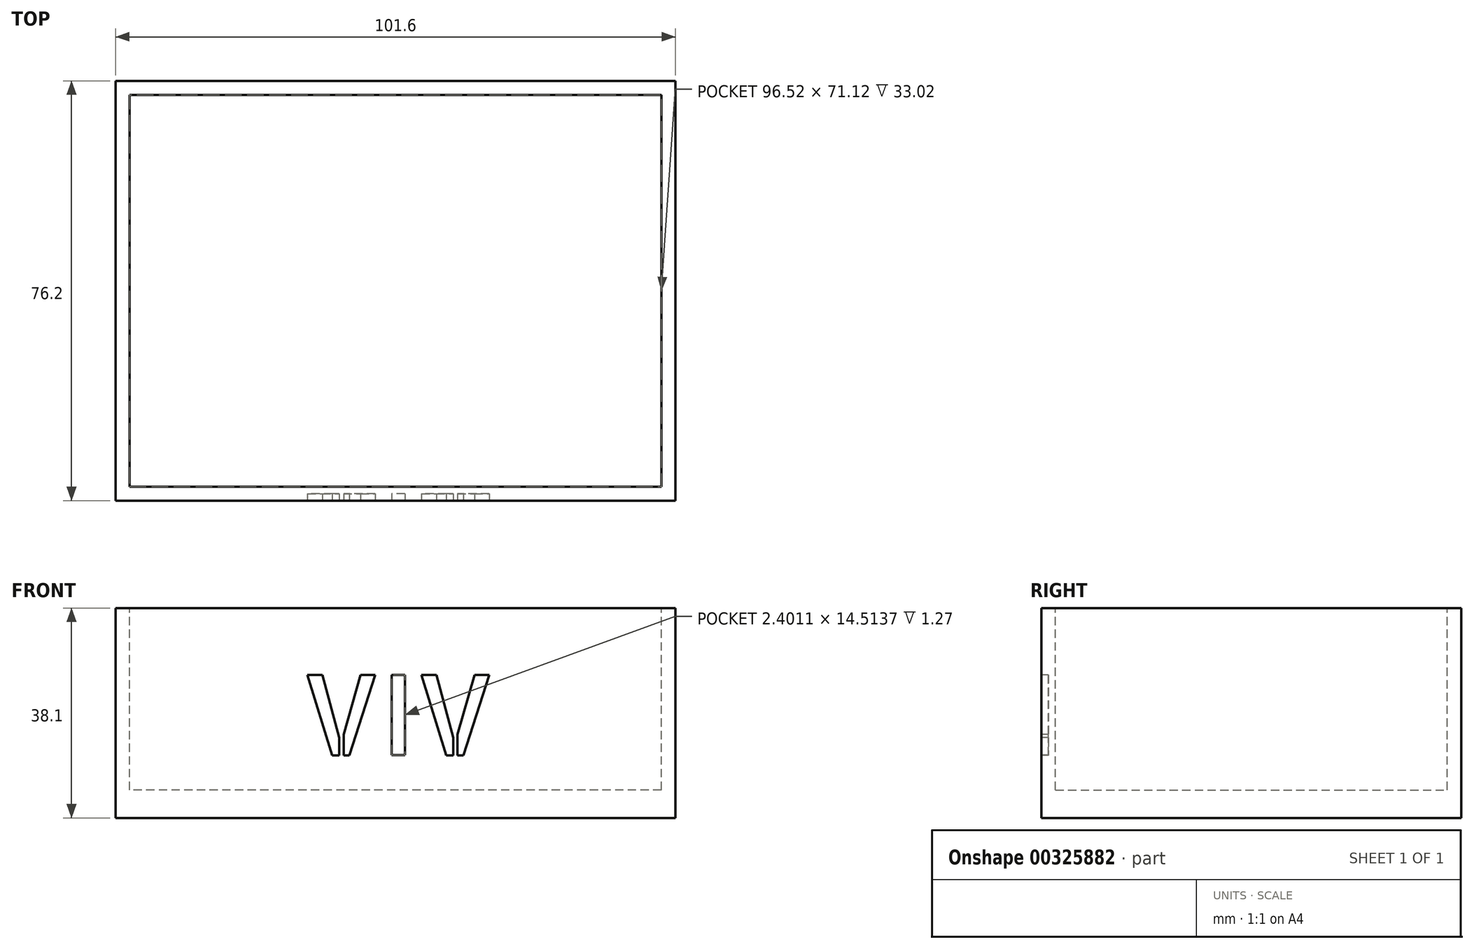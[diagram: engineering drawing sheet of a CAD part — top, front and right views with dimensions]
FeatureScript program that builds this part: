
annotation { "Feature Type Name" : "Feature", "Feature Type Description" : "" }
export const myFeature = defineFeature(function(context is Context, id is Id, definition is map)
    precondition{}
    {
        {
            var Q0;
            Q0=qCreatedBy(makeId("Top.planeOp"),FACE);
            var sketch = newSketch(context, id + "F0", { "sketchPlane" : qUnion([Q0])});
            skLineSegment(sketch, "E0.bottom", {"start": v(-50.8, 38.1) * mm, "end": v(50.8, 38.1) * mm});
            skLineSegment(sketch, "E0.top", {"start": v(-50.8, -38.1) * mm, "end": v(50.8, -38.1) * mm});
            skLineSegment(sketch, "E0.left", {"start": v(-50.8, 38.1) * mm, "end": v(-50.8, -38.1) * mm});
            skLineSegment(sketch, "E0.right", {"start": v(50.8, 38.1) * mm, "end": v(50.8, -38.1) * mm});
            skPoint(sketch, "E0.middle", {"position": v(0, 0) * mm});
            skSolve(sketch);
        }
        {
            var Q0;
            Q0=makeQuery(id+"F0.imprint","IMPRINT",FACE,{"disambiguationData":[TD([[makeQuery(id+"F0.imprint","IMPRINT",EDGE,{"derivedFrom":sQuery(id+"F0.wireOp",EDGE,"E0.bottom")}),-1.0]])]});
            extrude(context, id + "F1", {"entities" : qUnion([Q0]), "depth" : 38.1 * mm});
        }
        {
            var Q0;
            Q0=makeQuery(id+"F1.opExtrude","CAP_FACE",FACE,{"disambiguationData":[OSD([sQuery(id+"F0.wireOp",EDGE,"E0.bottom"),sQuery(id+"F0.wireOp",EDGE,"E0.top"),sQuery(id+"F0.wireOp",EDGE,"E0.left"),sQuery(id+"F0.wireOp",EDGE,"E0.right")])],"isStart":false});
            var sketch = newSketch(context, id + "F2", { "sketchPlane" : qUnion([Q0])});
            skLineSegment(sketch, "E1.bottom", {"start": v(48.26, -35.56) * mm, "end": v(-48.26, -35.56) * mm});
            skLineSegment(sketch, "E1.top", {"start": v(48.26, 35.56) * mm, "end": v(-48.26, 35.56) * mm});
            skLineSegment(sketch, "E1.left", {"start": v(48.26, -35.56) * mm, "end": v(48.26, 35.56) * mm});
            skLineSegment(sketch, "E1.right", {"start": v(-48.26, -35.56) * mm, "end": v(-48.26, 35.56) * mm});
            skPoint(sketch, "E1.middle", {"position": v(0, 0) * mm});
            skSolve(sketch);
        }
        {
            var Q0;
            Q0 = qSketchRegion(id + "F2", true);
            extrude(context, id + "F3", {"entities" : qUnion([Q0]), "operationType" : NewBodyOperationType.REMOVE, "oppositeDirection" : true, "depth" : 33.02 * mm});
        }
        {
            var Q0;
            Q0=makeQuery(id+"F1.opExtrude","SWEPT_FACE",FACE,{"disambiguationData":[OSD([sQuery(id+"F0.wireOp",EDGE,"E0.top")])]});
            var sketch = newSketch(context, id + "F4", { "sketchPlane" : qUnion([Q0])});
            skText(sketch, "E2", { "text": "VIV", "fontName": "AllertaStencil-Regular.ttf"});
            const initialGuessF4  = {"E2": [-0.01716, 0.01142, 1, 0, 0.01452]};
            skSetInitialGuess(sketch, initialGuessF4);
            skSolve(sketch);
        }
        {
            var Q0;
            Q0 = qSketchRegion(id + "F4", true);
            extrude(context, id + "F5", {"entities" : qUnion([Q0]), "operationType" : NewBodyOperationType.REMOVE, "oppositeDirection" : true, "depth" : 1.27 * mm});
        }
    });
